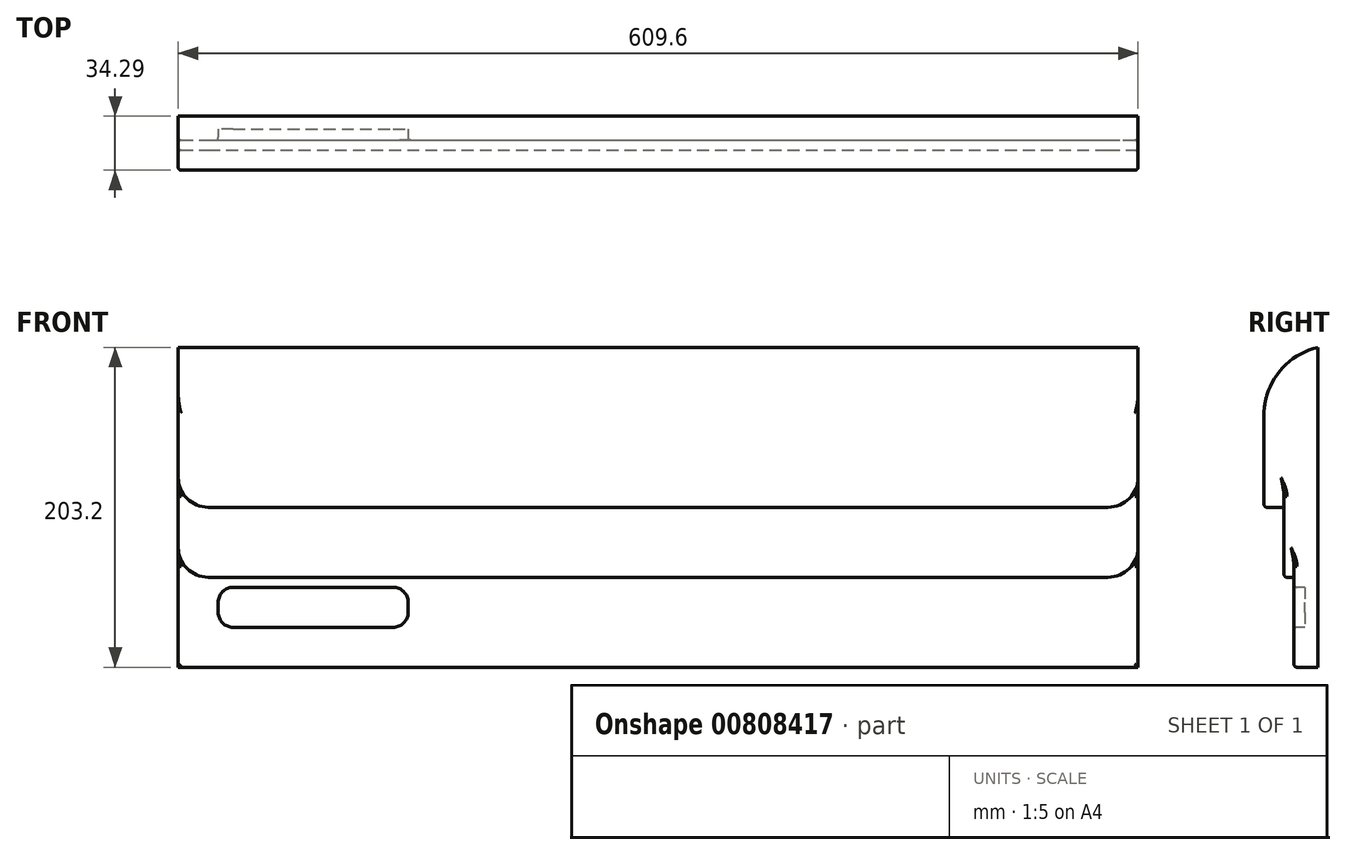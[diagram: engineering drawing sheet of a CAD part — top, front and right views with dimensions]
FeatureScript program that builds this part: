
annotation { "Feature Type Name" : "Feature", "Feature Type Description" : "" }
export const myFeature = defineFeature(function(context is Context, id is Id, definition is map)
    precondition{}
    {
        {
            var Q0;
            Q0=qCreatedBy(makeId("Front.planeOp"),FACE);
            var sketch = newSketch(context, id + "F0", { "sketchPlane" : qUnion([Q0])});
            skLineSegment(sketch, "E0.bottom", {"start": v(0, 0) * mm, "end": v(609.6, 0) * mm});
            skLineSegment(sketch, "E0.top", {"start": v(0, 203.2) * mm, "end": v(609.6, 203.2) * mm});
            skLineSegment(sketch, "E0.left", {"start": v(0, 0) * mm, "end": v(0, 203.2) * mm});
            skLineSegment(sketch, "E0.right", {"start": v(609.6, 0) * mm, "end": v(609.6, 203.2) * mm});
            skPoint(sketch, "E1.visualSharp", {"position": v(0, 203.2) * mm});
            skLineSegment(sketch, "E1.filletArc", {"start": v(0, 203.2) * mm, "end": v(0, 203.2) * mm});
            skPoint(sketch, "E2.visualSharp", {"position": v(0, 0) * mm});
            skLineSegment(sketch, "E2.filletArc", {"start": v(0, 0) * mm, "end": v(0, 0) * mm});
            skPoint(sketch, "E3.visualSharp", {"position": v(609.6, 203.2) * mm});
            skLineSegment(sketch, "E3.filletArc", {"start": v(609.6, 203.2) * mm, "end": v(609.6, 203.2) * mm});
            skPoint(sketch, "E4.visualSharp", {"position": v(609.6, 0) * mm});
            skLineSegment(sketch, "E4.filletArc", {"start": v(609.6, 0) * mm, "end": v(609.6, 0) * mm});
            skSolve(sketch);
        }
        {
            var Q0;
            Q0=makeQuery(id+"F0.imprint","IMPRINT",FACE,{"disambiguationData":[TD([[makeQuery(id+"F0.imprint","IMPRINT",EDGE,{"derivedFrom":sQuery(id+"F0.wireOp",EDGE,"E0.bottom")}),1.0]])]});
            extrude(context, id + "F1", {"entities" : qUnion([Q0]), "depth" : 15.24 * mm, "offsetDistance" : 25.4 * mm});
        }
        {
            var Q0;
            Q0=makeQuery(id+"F1.opExtrude","CAP_FACE",FACE,{"disambiguationData":[OSD([sQuery(id+"F0.wireOp",EDGE,"E0.bottom"),sQuery(id+"F0.wireOp",EDGE,"E0.top"),sQuery(id+"F0.wireOp",EDGE,"E0.left"),sQuery(id+"F0.wireOp",EDGE,"E0.right"),sQuery(id+"F0.wireOp",EDGE,"E1.filletArc"),sQuery(id+"F0.wireOp",EDGE,"E2.filletArc"),sQuery(id+"F0.wireOp",EDGE,"E3.filletArc"),sQuery(id+"F0.wireOp",EDGE,"E4.filletArc")])],"isStart":false});
            var sketch = newSketch(context, id + "F2", { "sketchPlane" : qUnion([Q0])});
            skLineSegment(sketch, "E5", {"start": v(304.8, 203.2) * mm, "end": v(304.8, 0) * mm});
            skLineSegment(sketch, "E6", {"start": v(0, 101.6) * mm, "end": v(304.8, 101.6) * mm, "construction": true});
            skLineSegment(sketch, "E7.bottom", {"start": v(34.93, 25.4) * mm, "end": v(136.53, 25.4) * mm});
            skLineSegment(sketch, "E7.top", {"start": v(34.93, 50.8) * mm, "end": v(136.53, 50.8) * mm});
            skLineSegment(sketch, "E7.left", {"start": v(25.4, 34.93) * mm, "end": v(25.4, 41.27) * mm});
            skLineSegment(sketch, "E7.right", {"start": v(146.05, 34.93) * mm, "end": v(146.05, 41.27) * mm});
            skPoint(sketch, "E8.visualSharp", {"position": v(25.4, 50.8) * mm});
            skArc(sketch, "E8.filletArc", {"start": v(34.93, 50.8) * mm, "mid": v(28.19, 48.01) * mm, "end": v(25.4, 41.27) * mm});
            skPoint(sketch, "E9.visualSharp", {"position": v(25.4, 25.4) * mm});
            skArc(sketch, "E9.filletArc", {"start": v(25.4, 34.93) * mm, "mid": v(28.19, 28.19) * mm, "end": v(34.93, 25.4) * mm});
            skPoint(sketch, "E10.visualSharp", {"position": v(146.05, 50.8) * mm});
            skArc(sketch, "E10.filletArc", {"start": v(146.05, 41.27) * mm, "mid": v(143.26, 48.01) * mm, "end": v(136.53, 50.8) * mm});
            skPoint(sketch, "E11.visualSharp", {"position": v(146.05, 25.4) * mm});
            skArc(sketch, "E11.filletArc", {"start": v(136.53, 25.4) * mm, "mid": v(143.26, 28.19) * mm, "end": v(146.05, 34.93) * mm});
            skLineSegment(sketch, "E12", {"start": v(152.4, 203.2) * mm, "end": v(152.4, 0) * mm, "construction": true});
            skLineSegment(sketch, "E13.MirrorCS", {"start": v(269.88, 50.8) * mm, "end": v(168.28, 50.8) * mm});
            skArc(sketch, "E14.MirrorCS", {"start": v(158.75, 41.27) * mm, "mid": v(161.54, 48.01) * mm, "end": v(168.28, 50.8) * mm});
            skArc(sketch, "E15.MirrorCS", {"start": v(168.28, 25.4) * mm, "mid": v(161.54, 28.19) * mm, "end": v(158.75, 34.93) * mm});
            skLineSegment(sketch, "E16.MirrorCS", {"start": v(269.88, 25.4) * mm, "end": v(168.28, 25.4) * mm});
            skArc(sketch, "E17.MirrorCS", {"start": v(279.4, 34.93) * mm, "mid": v(276.61, 28.19) * mm, "end": v(269.88, 25.4) * mm});
            skArc(sketch, "E18.MirrorCS", {"start": v(269.88, 50.8) * mm, "mid": v(276.61, 48.01) * mm, "end": v(279.4, 41.28) * mm});
            skLineSegment(sketch, "E19.0.1.0", {"start": v(34.93, 95.25) * mm, "end": v(136.53, 95.25) * mm});
            skArc(sketch, "E19.0.1.1", {"start": v(146.05, 85.72) * mm, "mid": v(143.26, 92.46) * mm, "end": v(136.53, 95.25) * mm});
            skArc(sketch, "E19.0.1.2", {"start": v(136.53, 69.85) * mm, "mid": v(143.26, 72.64) * mm, "end": v(146.05, 79.38) * mm});
            skLineSegment(sketch, "E19.0.1.3", {"start": v(34.93, 69.85) * mm, "end": v(136.53, 69.85) * mm});
            skArc(sketch, "E19.0.1.4", {"start": v(25.4, 79.38) * mm, "mid": v(28.19, 72.64) * mm, "end": v(34.93, 69.85) * mm});
            skArc(sketch, "E19.0.1.5", {"start": v(34.93, 95.25) * mm, "mid": v(28.19, 92.46) * mm, "end": v(25.4, 85.72) * mm});
            skLineSegment(sketch, "E19.0.1.6", {"start": v(269.88, 95.25) * mm, "end": v(168.28, 95.25) * mm});
            skArc(sketch, "E19.0.1.7", {"start": v(158.75, 85.72) * mm, "mid": v(161.54, 92.46) * mm, "end": v(168.28, 95.25) * mm});
            skArc(sketch, "E19.0.1.8", {"start": v(168.28, 69.85) * mm, "mid": v(161.54, 72.64) * mm, "end": v(158.75, 79.38) * mm});
            skLineSegment(sketch, "E19.0.1.9", {"start": v(269.88, 69.85) * mm, "end": v(168.28, 69.85) * mm});
            skArc(sketch, "E19.0.1.10", {"start": v(279.4, 79.38) * mm, "mid": v(276.61, 72.64) * mm, "end": v(269.88, 69.85) * mm});
            skArc(sketch, "E19.0.1.11", {"start": v(269.88, 95.25) * mm, "mid": v(276.61, 92.46) * mm, "end": v(279.4, 85.73) * mm});
            skLineSegment(sketch, "E19.1.0.0", {"start": v(34.92, 50.8) * mm, "end": v(136.53, 50.8) * mm});
            skArc(sketch, "E19.1.0.5", {"start": v(34.92, 50.8) * mm, "mid": v(28.19, 48.01) * mm, "end": v(25.4, 41.27) * mm});
            skLineSegment(sketch, "E19.1.1.0", {"start": v(34.92, 95.25) * mm, "end": v(136.53, 95.25) * mm});
            skArc(sketch, "E19.1.1.1", {"start": v(146.05, 85.72) * mm, "mid": v(143.26, 92.46) * mm, "end": v(136.53, 95.25) * mm});
            skArc(sketch, "E19.1.1.2", {"start": v(136.53, 69.85) * mm, "mid": v(143.26, 72.64) * mm, "end": v(146.05, 79.38) * mm});
            skLineSegment(sketch, "E19.1.1.3", {"start": v(34.92, 69.85) * mm, "end": v(136.53, 69.85) * mm});
            skArc(sketch, "E19.1.1.4", {"start": v(25.4, 79.38) * mm, "mid": v(28.19, 72.64) * mm, "end": v(34.92, 69.85) * mm});
            skArc(sketch, "E19.1.1.5", {"start": v(34.92, 95.25) * mm, "mid": v(28.19, 92.46) * mm, "end": v(25.4, 85.72) * mm});
            skLineSegment(sketch, "E19.1.1.6", {"start": v(269.88, 95.25) * mm, "end": v(168.28, 95.25) * mm});
            skArc(sketch, "E19.1.1.7", {"start": v(158.75, 85.72) * mm, "mid": v(161.54, 92.46) * mm, "end": v(168.28, 95.25) * mm});
            skArc(sketch, "E19.1.1.8", {"start": v(168.28, 69.85) * mm, "mid": v(161.54, 72.64) * mm, "end": v(158.75, 79.38) * mm});
            skLineSegment(sketch, "E19.1.1.9", {"start": v(269.88, 69.85) * mm, "end": v(168.28, 69.85) * mm});
            skArc(sketch, "E19.1.1.10", {"start": v(279.4, 79.38) * mm, "mid": v(276.61, 72.64) * mm, "end": v(269.88, 69.85) * mm});
            skArc(sketch, "E19.1.1.11", {"start": v(269.88, 95.25) * mm, "mid": v(276.61, 92.46) * mm, "end": v(279.4, 85.73) * mm});
            skLineSegment(sketch, "E19.2.0.0", {"start": v(34.92, 50.8) * mm, "end": v(136.53, 50.8) * mm});
            skArc(sketch, "E19.2.0.5", {"start": v(34.92, 50.8) * mm, "mid": v(28.19, 48.01) * mm, "end": v(25.4, 41.27) * mm});
            skLineSegment(sketch, "E19.2.1.0", {"start": v(34.92, 95.25) * mm, "end": v(136.53, 95.25) * mm});
            skArc(sketch, "E19.2.1.1", {"start": v(146.05, 85.72) * mm, "mid": v(143.26, 92.46) * mm, "end": v(136.53, 95.25) * mm});
            skArc(sketch, "E19.2.1.2", {"start": v(136.53, 69.85) * mm, "mid": v(143.26, 72.64) * mm, "end": v(146.05, 79.38) * mm});
            skLineSegment(sketch, "E19.2.1.3", {"start": v(34.92, 69.85) * mm, "end": v(136.53, 69.85) * mm});
            skArc(sketch, "E19.2.1.4", {"start": v(25.4, 79.38) * mm, "mid": v(28.19, 72.64) * mm, "end": v(34.92, 69.85) * mm});
            skArc(sketch, "E19.2.1.5", {"start": v(34.92, 95.25) * mm, "mid": v(28.19, 92.46) * mm, "end": v(25.4, 85.72) * mm});
            skLineSegment(sketch, "E19.2.1.6", {"start": v(269.88, 95.25) * mm, "end": v(168.28, 95.25) * mm});
            skArc(sketch, "E19.2.1.7", {"start": v(158.75, 85.72) * mm, "mid": v(161.54, 92.46) * mm, "end": v(168.28, 95.25) * mm});
            skArc(sketch, "E19.2.1.8", {"start": v(168.28, 69.85) * mm, "mid": v(161.54, 72.64) * mm, "end": v(158.75, 79.38) * mm});
            skLineSegment(sketch, "E19.2.1.9", {"start": v(269.88, 69.85) * mm, "end": v(168.28, 69.85) * mm});
            skArc(sketch, "E19.2.1.10", {"start": v(279.4, 79.38) * mm, "mid": v(276.61, 72.64) * mm, "end": v(269.88, 69.85) * mm});
            skArc(sketch, "E19.2.1.11", {"start": v(269.88, 95.25) * mm, "mid": v(276.61, 92.46) * mm, "end": v(279.4, 85.73) * mm});
            skLineSegment(sketch, "E19.direction1", {"start": v(34.93, 50.8) * mm, "end": v(34.92, 50.8) * mm});
            skLineSegment(sketch, "E19.direction2", {"start": v(34.93, 50.8) * mm, "end": v(34.93, 95.25) * mm, "construction": true});
            skLineSegment(sketch, "E20.0.1.0", {"start": v(34.93, 139.7) * mm, "end": v(136.53, 139.7) * mm});
            skArc(sketch, "E20.0.1.1", {"start": v(34.92, 139.7) * mm, "mid": v(28.19, 136.91) * mm, "end": v(25.4, 130.17) * mm});
            skArc(sketch, "E20.0.1.2", {"start": v(25.4, 123.83) * mm, "mid": v(28.19, 117.09) * mm, "end": v(34.92, 114.3) * mm});
            skLineSegment(sketch, "E20.0.1.3", {"start": v(34.92, 114.3) * mm, "end": v(136.53, 114.3) * mm});
            skArc(sketch, "E20.0.1.4", {"start": v(136.53, 114.3) * mm, "mid": v(143.26, 117.09) * mm, "end": v(146.05, 123.83) * mm});
            skArc(sketch, "E20.0.1.5", {"start": v(146.05, 130.17) * mm, "mid": v(143.26, 136.91) * mm, "end": v(136.53, 139.7) * mm});
            skArc(sketch, "E20.0.1.6", {"start": v(158.75, 130.17) * mm, "mid": v(161.54, 136.91) * mm, "end": v(168.28, 139.7) * mm});
            skArc(sketch, "E20.0.1.7", {"start": v(168.28, 114.3) * mm, "mid": v(161.54, 117.09) * mm, "end": v(158.75, 123.83) * mm});
            skLineSegment(sketch, "E20.0.1.8", {"start": v(269.88, 114.3) * mm, "end": v(168.28, 114.3) * mm});
            skLineSegment(sketch, "E20.0.1.9", {"start": v(269.88, 139.7) * mm, "end": v(168.28, 139.7) * mm});
            skArc(sketch, "E20.0.1.10", {"start": v(269.88, 139.7) * mm, "mid": v(276.61, 136.91) * mm, "end": v(279.4, 130.17) * mm});
            skArc(sketch, "E20.0.1.11", {"start": v(279.4, 123.83) * mm, "mid": v(276.61, 117.09) * mm, "end": v(269.88, 114.3) * mm});
            skLineSegment(sketch, "E20.1.1.0", {"start": v(34.92, 139.7) * mm, "end": v(136.53, 139.7) * mm});
            skArc(sketch, "E20.1.1.1", {"start": v(34.92, 139.7) * mm, "mid": v(28.19, 136.91) * mm, "end": v(25.4, 130.17) * mm});
            skArc(sketch, "E20.1.1.2", {"start": v(25.4, 123.83) * mm, "mid": v(28.19, 117.09) * mm, "end": v(34.92, 114.3) * mm});
            skLineSegment(sketch, "E20.1.1.3", {"start": v(34.92, 114.3) * mm, "end": v(136.53, 114.3) * mm});
            skArc(sketch, "E20.1.1.4", {"start": v(136.53, 114.3) * mm, "mid": v(143.26, 117.09) * mm, "end": v(146.05, 123.83) * mm});
            skArc(sketch, "E20.1.1.5", {"start": v(146.05, 130.17) * mm, "mid": v(143.26, 136.91) * mm, "end": v(136.53, 139.7) * mm});
            skArc(sketch, "E20.1.1.6", {"start": v(158.75, 130.17) * mm, "mid": v(161.54, 136.91) * mm, "end": v(168.28, 139.7) * mm});
            skArc(sketch, "E20.1.1.7", {"start": v(168.28, 114.3) * mm, "mid": v(161.54, 117.09) * mm, "end": v(158.75, 123.83) * mm});
            skLineSegment(sketch, "E20.1.1.8", {"start": v(269.88, 114.3) * mm, "end": v(168.28, 114.3) * mm});
            skLineSegment(sketch, "E20.1.1.9", {"start": v(269.88, 139.7) * mm, "end": v(168.28, 139.7) * mm});
            skArc(sketch, "E20.1.1.10", {"start": v(269.88, 139.7) * mm, "mid": v(276.61, 136.91) * mm, "end": v(279.4, 130.17) * mm});
            skArc(sketch, "E20.1.1.11", {"start": v(279.4, 123.83) * mm, "mid": v(276.61, 117.09) * mm, "end": v(269.88, 114.3) * mm});
            skLineSegment(sketch, "E20.2.0.0", {"start": v(34.92, 95.25) * mm, "end": v(136.52, 95.25) * mm});
            skLineSegment(sketch, "E20.2.0.3", {"start": v(34.92, 69.85) * mm, "end": v(136.52, 69.85) * mm});
            skArc(sketch, "E20.2.0.4", {"start": v(136.52, 69.85) * mm, "mid": v(143.26, 72.64) * mm, "end": v(146.05, 79.38) * mm});
            skArc(sketch, "E20.2.0.5", {"start": v(146.05, 85.72) * mm, "mid": v(143.26, 92.46) * mm, "end": v(136.52, 95.25) * mm});
            skArc(sketch, "E20.2.0.6", {"start": v(158.75, 85.72) * mm, "mid": v(161.54, 92.46) * mm, "end": v(168.27, 95.25) * mm});
            skArc(sketch, "E20.2.0.7", {"start": v(168.27, 69.85) * mm, "mid": v(161.54, 72.64) * mm, "end": v(158.75, 79.38) * mm});
            skLineSegment(sketch, "E20.2.0.8", {"start": v(269.88, 69.85) * mm, "end": v(168.27, 69.85) * mm});
            skLineSegment(sketch, "E20.2.0.9", {"start": v(269.88, 95.25) * mm, "end": v(168.27, 95.25) * mm});
            skLineSegment(sketch, "E20.2.1.0", {"start": v(34.92, 139.7) * mm, "end": v(136.52, 139.7) * mm});
            skArc(sketch, "E20.2.1.1", {"start": v(34.92, 139.7) * mm, "mid": v(28.19, 136.91) * mm, "end": v(25.4, 130.17) * mm});
            skArc(sketch, "E20.2.1.2", {"start": v(25.4, 123.83) * mm, "mid": v(28.19, 117.09) * mm, "end": v(34.92, 114.3) * mm});
            skLineSegment(sketch, "E20.2.1.3", {"start": v(34.92, 114.3) * mm, "end": v(136.52, 114.3) * mm});
            skArc(sketch, "E20.2.1.4", {"start": v(136.52, 114.3) * mm, "mid": v(143.26, 117.09) * mm, "end": v(146.05, 123.83) * mm});
            skArc(sketch, "E20.2.1.5", {"start": v(146.05, 130.17) * mm, "mid": v(143.26, 136.91) * mm, "end": v(136.52, 139.7) * mm});
            skArc(sketch, "E20.2.1.6", {"start": v(158.75, 130.17) * mm, "mid": v(161.54, 136.91) * mm, "end": v(168.27, 139.7) * mm});
            skArc(sketch, "E20.2.1.7", {"start": v(168.27, 114.3) * mm, "mid": v(161.54, 117.09) * mm, "end": v(158.75, 123.83) * mm});
            skLineSegment(sketch, "E20.2.1.8", {"start": v(269.88, 114.3) * mm, "end": v(168.27, 114.3) * mm});
            skLineSegment(sketch, "E20.2.1.9", {"start": v(269.88, 139.7) * mm, "end": v(168.27, 139.7) * mm});
            skArc(sketch, "E20.2.1.10", {"start": v(269.88, 139.7) * mm, "mid": v(276.61, 136.91) * mm, "end": v(279.4, 130.17) * mm});
            skArc(sketch, "E20.2.1.11", {"start": v(279.4, 123.83) * mm, "mid": v(276.61, 117.09) * mm, "end": v(269.88, 114.3) * mm});
            skLineSegment(sketch, "E20.direction1", {"start": v(34.93, 95.25) * mm, "end": v(34.92, 95.25) * mm});
            skLineSegment(sketch, "E20.direction2", {"start": v(34.93, 95.25) * mm, "end": v(34.93, 139.7) * mm, "construction": true});
            skLineSegment(sketch, "E21.MirrorCS", {"start": v(339.73, 139.7) * mm, "end": v(441.33, 139.7) * mm});
            skArc(sketch, "E22.MirrorCS", {"start": v(339.73, 139.7) * mm, "mid": v(332.99, 136.91) * mm, "end": v(330.2, 130.17) * mm});
            skArc(sketch, "E23.MirrorCS", {"start": v(330.2, 123.83) * mm, "mid": v(332.99, 117.09) * mm, "end": v(339.72, 114.3) * mm});
            skLineSegment(sketch, "E24.MirrorCS", {"start": v(339.72, 114.3) * mm, "end": v(441.32, 114.3) * mm});
            skArc(sketch, "E25.MirrorCS", {"start": v(441.32, 114.3) * mm, "mid": v(448.06, 117.09) * mm, "end": v(450.85, 123.83) * mm});
            skArc(sketch, "E26.MirrorCS", {"start": v(450.85, 130.18) * mm, "mid": v(448.06, 136.91) * mm, "end": v(441.33, 139.7) * mm});
            skArc(sketch, "E27.MirrorCS", {"start": v(463.55, 130.18) * mm, "mid": v(466.34, 136.91) * mm, "end": v(473.08, 139.7) * mm});
            skArc(sketch, "E28.MirrorCS", {"start": v(473.07, 114.3) * mm, "mid": v(466.34, 117.09) * mm, "end": v(463.55, 123.83) * mm});
            skLineSegment(sketch, "E29.MirrorCS", {"start": v(574.67, 114.3) * mm, "end": v(473.07, 114.3) * mm});
            skLineSegment(sketch, "E30.MirrorCS", {"start": v(574.68, 139.7) * mm, "end": v(473.08, 139.7) * mm});
            skArc(sketch, "E31.MirrorCS", {"start": v(574.68, 139.7) * mm, "mid": v(581.41, 136.91) * mm, "end": v(584.2, 130.18) * mm});
            skArc(sketch, "E32.MirrorCS", {"start": v(584.2, 123.83) * mm, "mid": v(581.41, 117.09) * mm, "end": v(574.67, 114.3) * mm});
            skLineSegment(sketch, "E33.MirrorCS", {"start": v(339.73, 95.25) * mm, "end": v(441.33, 95.25) * mm});
            skArc(sketch, "E34.MirrorCS", {"start": v(339.73, 95.25) * mm, "mid": v(332.99, 92.46) * mm, "end": v(330.2, 85.73) * mm});
            skArc(sketch, "E35.MirrorCS", {"start": v(330.2, 79.38) * mm, "mid": v(332.99, 72.64) * mm, "end": v(339.72, 69.85) * mm});
            skLineSegment(sketch, "E36.MirrorCS", {"start": v(339.72, 69.85) * mm, "end": v(441.32, 69.85) * mm});
            skArc(sketch, "E37.MirrorCS", {"start": v(441.32, 69.85) * mm, "mid": v(448.06, 72.64) * mm, "end": v(450.85, 79.38) * mm});
            skArc(sketch, "E38.MirrorCS", {"start": v(450.85, 85.73) * mm, "mid": v(448.06, 92.46) * mm, "end": v(441.33, 95.25) * mm});
            skArc(sketch, "E39.MirrorCS", {"start": v(473.07, 69.85) * mm, "mid": v(466.34, 72.64) * mm, "end": v(463.55, 79.38) * mm});
            skArc(sketch, "E40.MirrorCS", {"start": v(463.55, 85.73) * mm, "mid": v(466.34, 92.46) * mm, "end": v(473.08, 95.25) * mm});
            skLineSegment(sketch, "E41.MirrorCS", {"start": v(574.68, 95.25) * mm, "end": v(473.08, 95.25) * mm});
            skLineSegment(sketch, "E42.MirrorCS", {"start": v(574.67, 69.85) * mm, "end": v(473.07, 69.85) * mm});
            skArc(sketch, "E43.MirrorCS", {"start": v(584.2, 79.38) * mm, "mid": v(581.41, 72.64) * mm, "end": v(574.67, 69.85) * mm});
            skArc(sketch, "E44.MirrorCS", {"start": v(574.68, 95.25) * mm, "mid": v(581.41, 92.46) * mm, "end": v(584.2, 85.73) * mm});
            skLineSegment(sketch, "E45.MirrorCS", {"start": v(339.73, 50.8) * mm, "end": v(441.33, 50.8) * mm});
            skLineSegment(sketch, "E46.MirrorCS", {"start": v(339.72, 25.4) * mm, "end": v(441.32, 25.4) * mm});
            skArc(sketch, "E47.MirrorCS", {"start": v(330.2, 34.93) * mm, "mid": v(332.99, 28.19) * mm, "end": v(339.72, 25.4) * mm});
            skArc(sketch, "E48.MirrorCS", {"start": v(339.73, 50.8) * mm, "mid": v(332.99, 48.01) * mm, "end": v(330.2, 41.28) * mm});
            skArc(sketch, "E49.MirrorCS", {"start": v(450.85, 41.28) * mm, "mid": v(448.06, 48.01) * mm, "end": v(441.33, 50.8) * mm});
            skArc(sketch, "E50.MirrorCS", {"start": v(441.32, 25.4) * mm, "mid": v(448.06, 28.19) * mm, "end": v(450.85, 34.93) * mm});
            skArc(sketch, "E51.MirrorCS", {"start": v(473.07, 25.4) * mm, "mid": v(466.34, 28.19) * mm, "end": v(463.55, 34.93) * mm});
            skArc(sketch, "E52.MirrorCS", {"start": v(463.55, 41.28) * mm, "mid": v(466.34, 48.01) * mm, "end": v(473.08, 50.8) * mm});
            skLineSegment(sketch, "E53.MirrorCS", {"start": v(574.68, 50.8) * mm, "end": v(473.08, 50.8) * mm});
            skLineSegment(sketch, "E54.MirrorCS", {"start": v(574.67, 25.4) * mm, "end": v(473.07, 25.4) * mm});
            skArc(sketch, "E55.MirrorCS", {"start": v(574.68, 50.8) * mm, "mid": v(581.41, 48.01) * mm, "end": v(584.2, 41.28) * mm});
            skArc(sketch, "E56.MirrorCS", {"start": v(584.2, 34.93) * mm, "mid": v(581.41, 28.19) * mm, "end": v(574.67, 25.4) * mm});
            skSolve(sketch);
        }
        {
            var Q0;
            Q0=makeQuery(id+"F2.imprint","IMPRINT",FACE,{"disambiguationData":[TD([[makeQuery(id+"F2.imprint","IMPRINT",EDGE,{"derivedFrom":sQuery(id+"F2.wireOp",EDGE,"E20.2.1.0")}),-1.0]])]});
            var Q1;
            Q1=makeQuery(id+"F2.imprint","IMPRINT",FACE,{"disambiguationData":[TD([[makeQuery(id+"F2.imprint","IMPRINT",EDGE,{"derivedFrom":sQuery(id+"F2.wireOp",EDGE,"E20.2.1.6")}),-1.0]])]});
            var Q2;
            Q2=makeQuery(id+"F2.imprint","IMPRINT",FACE,{"disambiguationData":[TD([[makeQuery(id+"F2.imprint","IMPRINT",EDGE,{"derivedFrom":sQuery(id+"F2.wireOp",EDGE,"E20.2.0.6")}),-1.0]])]});
            var Q3;
            Q3=makeQuery(id+"F2.imprint","IMPRINT",FACE,{"disambiguationData":[TD([[makeQuery(id+"F2.imprint","IMPRINT",EDGE,{"derivedFrom":sQuery(id+"F2.wireOp",EDGE,"E20.2.0.0")}),-1.0]])]});
            var Q4;
            Q4=makeQuery(id+"F2.imprint","IMPRINT",FACE,{"disambiguationData":[TD([[makeQuery(id+"F2.imprint","IMPRINT",EDGE,{"derivedFrom":sQuery(id+"F2.wireOp",EDGE,"E19.2.0.0")}),-1.0]])]});
            var Q5;
            Q5=makeQuery(id+"F2.imprint","IMPRINT",FACE,{"disambiguationData":[TD([[makeQuery(id+"F2.imprint","IMPRINT",EDGE,{"derivedFrom":sQuery(id+"F2.wireOp",EDGE,"E13.MirrorCS")}),1.0]])]});
            var Q6;
            Q6=makeQuery(id+"F2.imprint","IMPRINT",FACE,{"disambiguationData":[TD([[makeQuery(id+"F2.imprint","IMPRINT",EDGE,{"derivedFrom":sQuery(id+"F2.wireOp",EDGE,"E21.MirrorCS")}),-1.0]])]});
            var Q7;
            Q7=makeQuery(id+"F2.imprint","IMPRINT",FACE,{"disambiguationData":[TD([[makeQuery(id+"F2.imprint","IMPRINT",EDGE,{"derivedFrom":sQuery(id+"F2.wireOp",EDGE,"E33.MirrorCS")}),-1.0]])]});
            var Q8;
            Q8=makeQuery(id+"F2.imprint","IMPRINT",FACE,{"disambiguationData":[TD([[makeQuery(id+"F2.imprint","IMPRINT",EDGE,{"derivedFrom":sQuery(id+"F2.wireOp",EDGE,"E45.MirrorCS")}),-1.0]])]});
            var Q9;
            Q9=makeQuery(id+"F2.imprint","IMPRINT",FACE,{"disambiguationData":[TD([[makeQuery(id+"F2.imprint","IMPRINT",EDGE,{"derivedFrom":sQuery(id+"F2.wireOp",EDGE,"E51.MirrorCS")}),-1.0]])]});
            var Q10;
            Q10=makeQuery(id+"F2.imprint","IMPRINT",FACE,{"disambiguationData":[TD([[makeQuery(id+"F2.imprint","IMPRINT",EDGE,{"derivedFrom":sQuery(id+"F2.wireOp",EDGE,"E39.MirrorCS")}),-1.0]])]});
            var Q11;
            Q11=makeQuery(id+"F2.imprint","IMPRINT",FACE,{"disambiguationData":[TD([[makeQuery(id+"F2.imprint","IMPRINT",EDGE,{"derivedFrom":sQuery(id+"F2.wireOp",EDGE,"E27.MirrorCS")}),-1.0]])]});
            extrude(context, id + "F3", {"entities" : qUnion([Q0, Q1, Q2, Q3, Q4, Q5, Q6, Q7, Q8, Q9, Q10, Q11]), "operationType" : NewBodyOperationType.REMOVE, "oppositeDirection" : true, "depth" : 7 * mm, "offsetDistance" : 25.4 * mm});
        }
        {
            var Q0;
            Q0=makeQuery(id+"F1.opExtrude","CAP_FACE",FACE,{"disambiguationData":[OSD([sQuery(id+"F0.wireOp",EDGE,"E0.bottom"),sQuery(id+"F0.wireOp",EDGE,"E0.top"),sQuery(id+"F0.wireOp",EDGE,"E0.left"),sQuery(id+"F0.wireOp",EDGE,"E0.right"),sQuery(id+"F0.wireOp",EDGE,"E1.filletArc"),sQuery(id+"F0.wireOp",EDGE,"E2.filletArc"),sQuery(id+"F0.wireOp",EDGE,"E3.filletArc"),sQuery(id+"F0.wireOp",EDGE,"E4.filletArc")])],"isStart":false});
            var sketch = newSketch(context, id + "F4", { "sketchPlane" : qUnion([Q0])});
            skLineSegment(sketch, "E57", {"start": v(19.05, 57.15) * mm, "end": v(590.55, 57.15) * mm});
            skLineSegment(sketch, "E58", {"start": v(0, 101.6) * mm, "end": v(609.6, 101.6) * mm});
            skLineSegment(sketch, "E59", {"start": v(0, 101.6) * mm, "end": v(0, 76.2) * mm});
            skLineSegment(sketch, "E60", {"start": v(609.6, 101.6) * mm, "end": v(609.6, 76.2) * mm});
            skPoint(sketch, "E61.visualSharp", {"position": v(0, 57.15) * mm});
            skArc(sketch, "E61.filletArc", {"start": v(0, 76.2) * mm, "mid": v(5.58, 62.73) * mm, "end": v(19.05, 57.15) * mm});
            skPoint(sketch, "E62.visualSharp", {"position": v(609.6, 57.15) * mm});
            skArc(sketch, "E62.filletArc", {"start": v(590.55, 57.15) * mm, "mid": v(604.02, 62.73) * mm, "end": v(609.6, 76.2) * mm});
            skLineSegment(sketch, "E63", {"start": v(0, 0) * mm, "end": v(0, 101.6) * mm});
            skLineSegment(sketch, "E64", {"start": v(609.6, 0) * mm, "end": v(609.6, 101.6) * mm});
            skSolve(sketch);
        }
        {
            var Q0;
            Q0=makeQuery(id+"F4.imprint","IMPRINT",FACE,{"disambiguationData":[TD([[makeQuery(id+"F4.imprint","IMPRINT",EDGE,{"derivedFrom":sQuery(id+"F4.wireOp",EDGE,"E57")}),1.0]])]});
            extrude(context, id + "F5", {"entities" : qUnion([Q0]), "operationType" : NewBodyOperationType.ADD, "depth" : 6.35 * mm, "offsetDistance" : 25.4 * mm});
        }
        {
            var Q0;
            {var subQ0=sQuery(id+"F0.wireOp",EDGE,"E1.filletArc");var subQ1=sQuery(id+"F0.wireOp",EDGE,"E0.right");var subQ2=sQuery(id+"F0.wireOp",EDGE,"E0.left");var subQ3=sQuery(id+"F0.wireOp",EDGE,"E0.top");var subQ4=sQuery(id+"F0.wireOp",EDGE,"E3.filletArc");Q0=makeQuery(id+"F5.boolean.opBoolean","SPLIT",FACE,{"disambiguationData":[TD([makeQuery(id+"F1.opExtrude","SWEPT_FACE",FACE,{"disambiguationData":[OSD([subQ3])]})])],"derivedFrom":makeQuery(id+"F1.opExtrude","CAP_FACE",FACE,{"disambiguationData":[OSD([sQuery(id+"F0.wireOp",EDGE,"E0.bottom"),subQ3,subQ2,subQ1,subQ0,sQuery(id+"F0.wireOp",EDGE,"E2.filletArc"),subQ4,sQuery(id+"F0.wireOp",EDGE,"E4.filletArc")])],"isStart":false})});}
            extrude(context, id + "F6", {"entities" : qUnion([Q0]), "operationType" : NewBodyOperationType.ADD, "depth" : 19.05 * mm, "offsetDistance" : 25.4 * mm});
        }
        {
            var Q0;
            Q0=makeQuery(id+"F6.opExtrude","SWEPT_EDGE",EDGE,{"disambiguationData":[OSD([sQuery(id+"F4.wireOp",EDGE,"E58"),sQuery(id+"F4.wireOp",EDGE,"E59"),sQuery(id+"F4.wireOp",EDGE,"E63")])]});
            var Q1;
            Q1=makeQuery(id+"F6.opExtrude","SWEPT_EDGE",EDGE,{"disambiguationData":[OSD([sQuery(id+"F4.wireOp",EDGE,"E58"),sQuery(id+"F4.wireOp",EDGE,"E60"),sQuery(id+"F4.wireOp",EDGE,"E64")])]});
            fillet(context, id + "F7", {"entities" : qUnion([Q0, Q1]), "radius" : 19.05 * mm, "tangentPropagation" : true, "allowEdgeOverflow" : false});
        }
        {
            var Q0;
            {var subQ0=sQuery(id+"F0.wireOp",EDGE,"E0.right");Q0=makeQuery(id+"F6.boolean.opBoolean","MERGE",FACE,{"derivedFrom":[makeQuery(id+"F5.boolean.opBoolean","MERGE",FACE,{"derivedFrom":[makeQuery(id+"F1.opExtrude","SWEPT_FACE",FACE,{"disambiguationData":[OSD([subQ0])]}),makeQuery(id+"F5.opExtrude","SWEPT_FACE",FACE,{"disambiguationData":[OSD([sQuery(id+"F4.wireOp",EDGE,"E64")])]})]}),makeQuery(id+"F6.opExtrude","SWEPT_FACE",FACE,{"disambiguationData":[OSD([subQ0])]})]});}
            var sketch = newSketch(context, id + "F8", { "sketchPlane" : qUnion([Q0])});
            skArc(sketch, "E65", {"start": v(0, 203.2) * mm, "mid": v(-24.08, 188.32) * mm, "end": v(-34.3, 161.92) * mm});
            skSolve(sketch);
        }
        {
            var Q0;
            {var subQ0=sQuery(id+"F8.wireOp",EDGE,"E65");Q0=makeQuery(id+"F8.imprint","IMPRINT",FACE,{"disambiguationData":[TD([[makeQuery(id+"F8.imprint","IMPRINT",EDGE,{"derivedFrom":subQ0}),-1.0]])]});}
            extrude(context, id + "F9", {"entities" : qUnion([Q0]), "operationType" : NewBodyOperationType.REMOVE, "endBound" : BoundingType.THROUGH_ALL, "oppositeDirection" : true, "depth" : 25.4 * mm, "offsetDistance" : 25.4 * mm});
        }
        {
            var Q0;
            Q0=makeQuery(id+"F6.opExtrude","CAP_FACE",FACE,{"disambiguationData":[OSD([sQuery(id+"F0.wireOp",EDGE,"E0.bottom"),sQuery(id+"F0.wireOp",EDGE,"E0.top"),sQuery(id+"F0.wireOp",EDGE,"E0.left"),sQuery(id+"F0.wireOp",EDGE,"E0.right")])],"isStart":false});
            var Q1;
            Q1=makeQuery(id+"F5.opExtrude","CAP_FACE",FACE,{"disambiguationData":[OSD([sQuery(id+"F4.wireOp",EDGE,"E57"),sQuery(id+"F4.wireOp",EDGE,"E58"),sQuery(id+"F4.wireOp",EDGE,"E61.filletArc"),sQuery(id+"F4.wireOp",EDGE,"E62.filletArc"),sQuery(id+"F4.wireOp",EDGE,"E63"),sQuery(id+"F4.wireOp",EDGE,"E64")])],"isStart":false});
            var Q2;
            {var subQ0=sQuery(id+"F0.wireOp",EDGE,"E0.bottom");var subQ1=sQuery(id+"F0.wireOp",EDGE,"E0.left");var subQ2=sQuery(id+"F0.wireOp",EDGE,"E0.right");Q2=makeQuery(id+"F5.boolean.opBoolean","SPLIT",FACE,{"disambiguationData":[TD([makeQuery(id+"F1.opExtrude","SWEPT_FACE",FACE,{"disambiguationData":[OSD([subQ0])]})])],"derivedFrom":makeQuery(id+"F1.opExtrude","CAP_FACE",FACE,{"disambiguationData":[OSD([subQ0,sQuery(id+"F0.wireOp",EDGE,"E0.top"),subQ1,subQ2])],"isStart":false})});}
            fillet(context, id + "F10", {"entities" : qUnion([Q0, Q1, Q2]), "radius" : 1.9 * mm, "tangentPropagation" : true, "allowEdgeOverflow" : false});
        }
    });
